# Revit family: KS ALU-PU 80 -s-, DS 50, M 8-M10, Ø 17,2- 35
name_source: partatom
category: HLS-Bauteile
revit_build: Autodesk Revit 2017 (Build: 20190507_1515(x64)
units: mm (PartAtom-declared; Revit-internal decimal feet)

## family parameters
Arbeitsebenenbasiert = Ja
Beim Laden mit Abzugskörper schneiden = Nein
Bemaßung runder Anschluss = Durchmesser verwenden
Gemeinsam genutzt = Ja
Immer vertikal = Nein
Raumberechnungspunkt = Nein
Teiletyp = Normal

## types (4) — shared parameters
A = 69 mm
Anschluss = M8/M10
BP = 14 mm  [stored 0.0459318 ft]
Baustoffklasse = B2
DS = 50 mm  [stored 0.164042 ft]
DVS = 5 mm  [stored 0.0164042 ft]
Dichte Kern = 80 kg/m³
Dichte Mantel = 2.700 kg/m³
Dicke Mantel = 0,08 mm
Dämmkörper = ALU/PU
Dämmstärke = 50 mm  [stored 0.164042 ft]
Fabrikat = MEFA
Firma = MEFA Befestigungs- und Montagesysteme GmbH
HGA = 16 mm  [stored 0.0524934 ft]
Kurztext1 = Kälteschelle RG80s ALU/PU
L = 40 mm  [stored 0.131234 ft]
L Ü Bogen = 19 mm
MB = 25 mm  [stored 0.082021 ft]
MD = 3 mm  [stored 0.00984252 ft]
Material = Stahl
Material Mantel = Alufolie
Materialname = DD11
Mengeneinheit = St
Oberflaeche = galvanisch verzinkt
Rohrschellentyp = Omnia MB
Schalenlänge = 40 mm
Vorgabe-Ansicht = 1219 mm
Wasserdampfdiffusionswiderstand = 18750 µ
Wärmeleitfähigkeit = 0.025 W/mK
d1 = 7 mm  [stored 0.0229659 ft]
max. Temperaturbeständigkeit = 120 °C
mittl. Nenndruckfestigkeit Kern = 0,5 N/mm²
stat. Belastung Kern = 0,1 N/mm²
vpe = 1 St

## per-type parameters (varying)
| type | AB | Anschlußhöhe | Artikelnummer | B | Breite | D | D0 | DF1 | DF2 | Dmax | Dmin | EAN | Gewicht | Gewicht pro Bauteil | H | Kurztext2 | R | RM | Rohraußendurchmesser Kupfer | Rohraußendurchmesser Stahl | S | S1 | max. zul. Last |
| Kälteschelle ALU-PU 80 -s-, DS 50, M8/M10, Ø 17,2 | 2 mm  [stored 0.00656168 ft] | 71 mm | 71701849 | 158 mm | 158 mm | 18 mm  [stored 0.0590551 ft] | 118 mm | 16 mm  [stored 0.0524934 ft] | 17 mm  [stored 0.0557743 ft] | 20 mm  [stored 0.0656168 ft] | 16 mm  [stored 0.0524934 ft] | 4250928441829 | 0.28 kg | 0.28 kg | 139 mm | 17,2 mm Iso 50 x 40 mm M8/M10 | 59 mm | 62 mm | 18 mm | 17,2 mm | 142 mm | 137 mm | 0.10 kN |
| Kälteschelle ALU-PU 80 -s-, DS 50, M8/M10, Ø 21,3 | 2 mm  [stored 0.00656168 ft] | 70 mm | 71702249 | 158 mm | 158 mm | 22 mm | 122 mm | 14 mm  [stored 0.0459318 ft] | 15 mm  [stored 0.0492126 ft] | 24 mm  [stored 0.0787402 ft] | 20 mm  [stored 0.0656168 ft] | 4250928441836 | 0.28 kg | 0.28 kg | 143 mm | 21,3 mm Iso 50 x 40 mm M8/M10 | 61 mm | 64 mm  [stored 0.209974 ft] | 22 mm | 21,3 mm | 144 mm | 141 mm | 0.10 kN |
| Kälteschelle ALU-PU 80 -s-, DS 50, M8/M10, Ø 26,9 | 2 mm  [stored 0.00656168 ft] | 69 mm | 71702849 | 168 mm | 165 mm | 28 mm  [stored 0.0918635 ft] | 128 mm  [stored 0.419948 ft] | 16 mm  [stored 0.0524934 ft] | 17 mm  [stored 0.0557743 ft] | 30 mm  [stored 0.0984252 ft] | 26 mm | 4250928441843 | 0.29 kg | 0.29 kg | 149 mm | 26,9 mm Iso 50 x 40 mm M8/M10 | 64 mm  [stored 0.209974 ft] | 67 mm | 28 mm | 26,9 mm | 152 mm | 147 mm | 0.20 kN |
| Kälteschelle ALU-PU 80 -s-, DS 50, M8/M10, Ø 33,7 | 3 mm  [stored 0.00984252 ft] | 70 mm | 71703449 | 177 mm | 175 mm | 35 mm | 135 mm  [stored 0.442913 ft] | 18 mm  [stored 0.0590551 ft] | 18 mm  [stored 0.0590551 ft] | 36 mm | 32 mm  [stored 0.104987 ft] | 4250928441850 | 0.30 kg | 0.30 kg | 156 mm | 33,7 mm Iso 50 x 40 mm M8/M10 | 68 mm | 70 mm | 35 mm | 33,7 mm | 159 mm | 154 mm | 0.20 kN |

note: [stored X ft] marks values corroborated as IEEE doubles in the binary element streams (Revit-internal decimal feet)

## geometry (parser evidence)
native form markers: Sweep x1
no freeform markers — native parametric forms only
